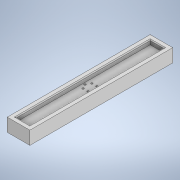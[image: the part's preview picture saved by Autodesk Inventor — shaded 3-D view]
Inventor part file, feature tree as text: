
AUTODESK INVENTOR PART (.ipt)
format: ipt  version: 2020 (Build 240168000, 168)  size: 135,168 bytes
history: native  units: mm
features: sketch x3, extrude x2, hole x1, pattern_circular x1, fillet x1, projected_geometry x1
ambient origin geometry x8: Origin, YZ Plane, XZ Plane, XY Plane, X Axis, Y Axis, Z Axis, Center Point
bodies: Solid1 (feature_tree)
feature tree (9):
  extrude  "Extrusion1"  Depth=305.0mm
  extrude  "Extrusion2"  Depth=10.0mm TaperAngle=0.0deg
  hole  "Hole2"  [1 undecoded]
  pattern_circular  "Circular Pattern1"  Count=6 Angle=360.0deg
  fillet  "Fillet1"  Radius=2.0mm
  sketch  "Sketch1"  dims[d0=31.4mm d1=305.0mm]
  sketch  "Sketch2"  dims[d2=10.0mm d3=10.0mm d4=0.0mm]
  projected_geometry  "Projected Loop1"
  sketch  "Sketch4"  dims[d5=20.0mm d6=0.0mm d14=11.5mm d15=4.134mm d16=10.0mm d17=6.5mm d18=4.0mm d19=14.3117mm d20=14.2mm d21=20.594885mm d22=60.0mm d23=360.0deg d25=2.0mm]
note: 1 required parameter value undecoded (feature->parameter linkage not recoverable at this tier; creation-order binding heuristic only, values carry confidence <= 0.55)
